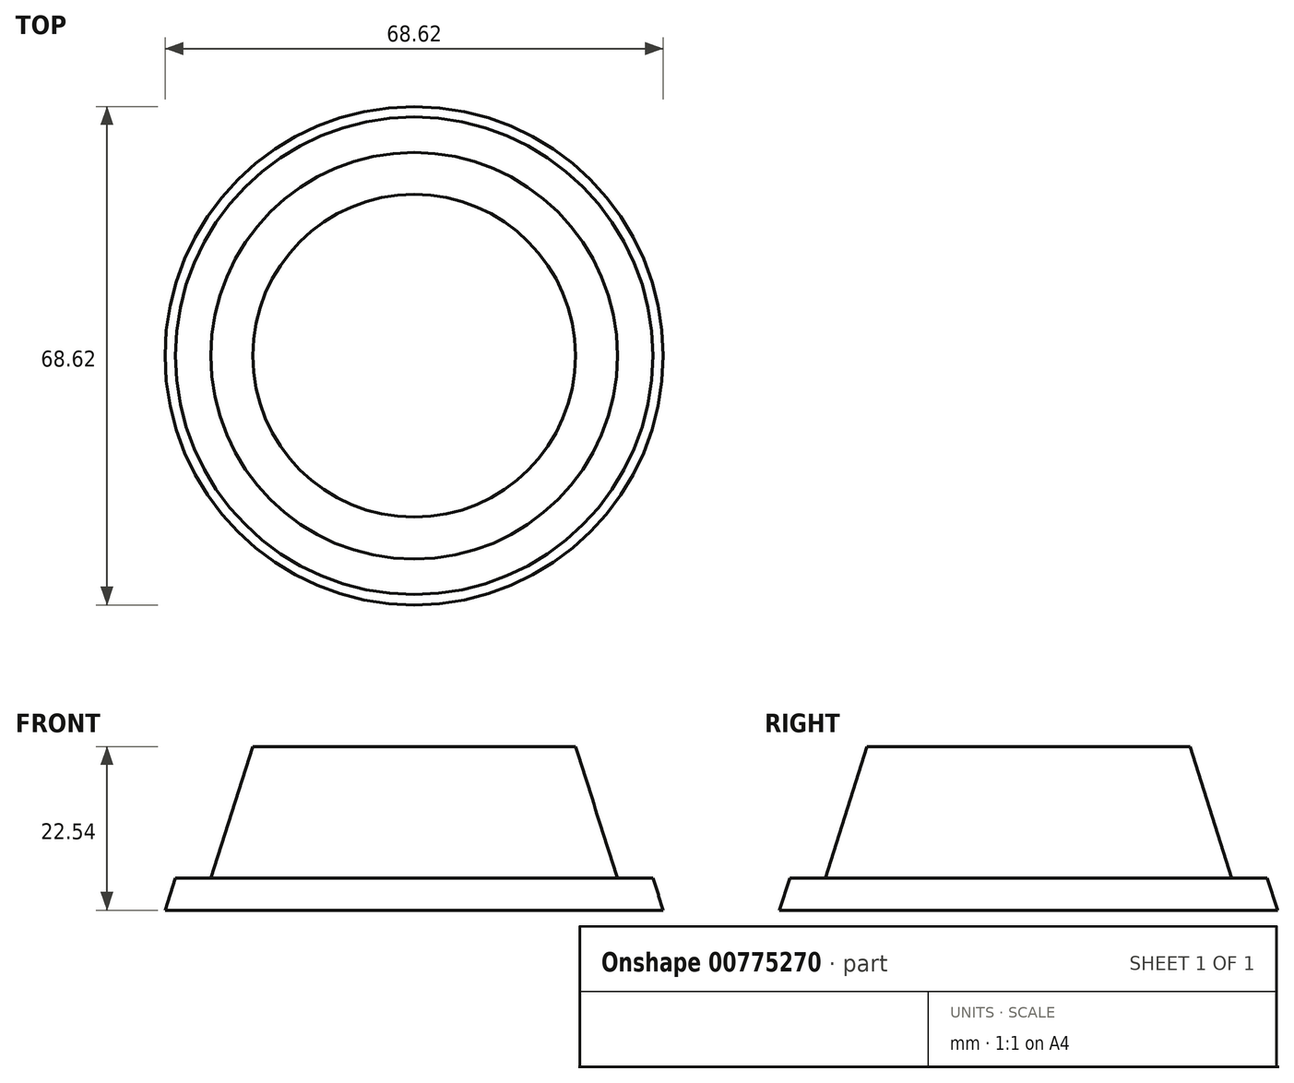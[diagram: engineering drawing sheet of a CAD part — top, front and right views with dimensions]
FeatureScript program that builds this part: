
annotation { "Feature Type Name" : "Feature", "Feature Type Description" : "" }
export const myFeature = defineFeature(function(context is Context, id is Id, definition is map)
    precondition{}
    {
        {
            var Q0;
            Q0=qCreatedBy(makeId("Front.planeOp"),FACE);
            var sketch = newSketch(context, id + "F0", { "sketchPlane" : qUnion([Q0])});
            skLineSegment(sketch, "E0", {"start": v(-24.83, 31.06) * mm, "end": v(-24.83, 0) * mm});
            skLineSegment(sketch, "E1", {"start": v(-24.83, 0) * mm, "end": v(34.76, 0) * mm});
            skPoint(sketch, "E2.start.orphan", {"position": v(0, 20.02) * mm});
            skLineSegment(sketch, "E3", {"start": v(3.17, 23.33) * mm, "end": v(8.06, 23.33) * mm});
            skLineSegment(sketch, "E4", {"start": v(8.06, 23.33) * mm, "end": v(9.48, 18.92) * mm});
            skPoint(sketch, "E5.end.orphan", {"position": v(0, 31.06) * mm});
            skLineSegment(sketch, "E6", {"start": v(-24.83, 31.06) * mm, "end": v(-24.83, 41.46) * mm});
            skPoint(sketch, "E7.orphan", {"position": v(-24.83, 56.44) * mm});
            skLineSegment(sketch, "E8", {"start": v(3.17, 23.33) * mm, "end": v(-24.83, 23.33) * mm});
            skLineSegment(sketch, "E9", {"start": v(9.48, 18.92) * mm, "end": v(-24.83, 18.92) * mm});
            skPoint(sketch, "E9.endSnap0", {"position": v(-24.83, 15.53) * mm});
            skLineSegment(sketch, "E10", {"start": v(-24.83, 41.46) * mm, "end": v(-2.6, 41.46) * mm});
            skLineSegment(sketch, "E11", {"start": v(-2.6, 41.46) * mm, "end": v(3.17, 23.33) * mm});
            skPoint(sketch, "E12.end.orphan", {"position": v(-24.83, 46.82) * mm});
            skSolve(sketch);
        }
        {
            var Q0;
            Q0 = qSketchRegion(id + "F0", true);
            var Q1;
            Q1=sQuery(id+"F0.wireOp",EDGE,"E0");
            revolve(context, id + "F1", {"surfaceOperationType" : NewSurfaceOperationType.NEW, "entities" : qUnion([Q0]), "axis" : qUnion([Q1]), "revolveType" : RevolveType.FULL});
        }
    });
